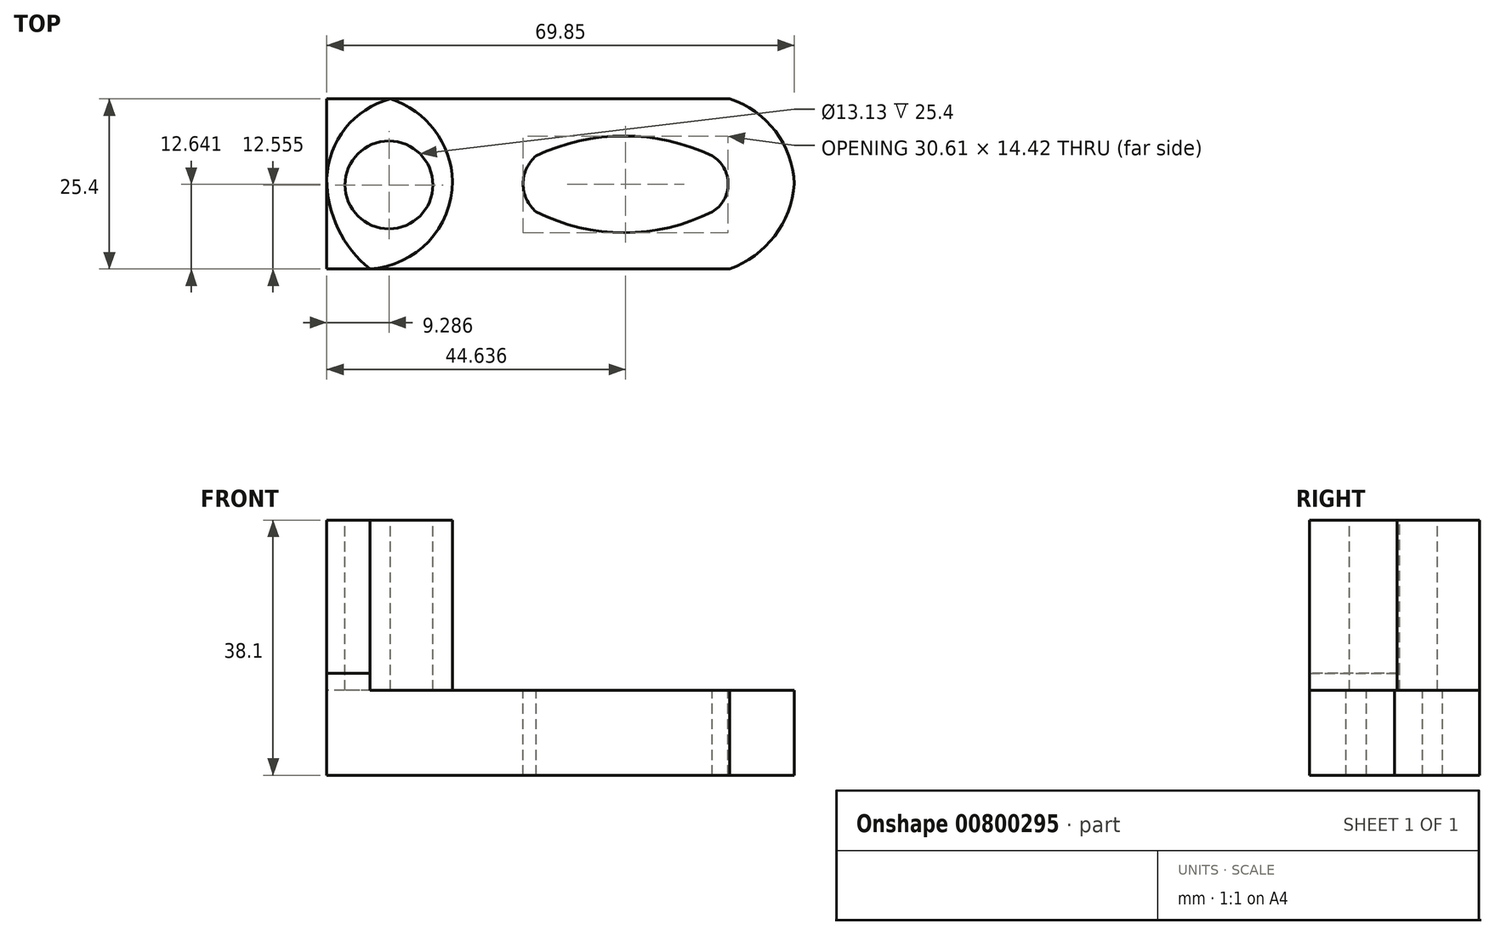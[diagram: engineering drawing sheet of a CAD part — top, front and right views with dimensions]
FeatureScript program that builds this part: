
annotation { "Feature Type Name" : "Feature", "Feature Type Description" : "" }
export const myFeature = defineFeature(function(context is Context, id is Id, definition is map)
    precondition{}
    {
        {
            var Q0;
            Q0=qCreatedBy(makeId("Front.planeOp"),FACE);
            var sketch = newSketch(context, id + "F0", { "sketchPlane" : qUnion([Q0])});
            skLineSegment(sketch, "E0", {"start": v(0, 0) * mm, "end": v(69.85, 0) * mm});
            skLineSegment(sketch, "E1", {"start": v(69.85, 0) * mm, "end": v(69.85, 12.7) * mm});
            skLineSegment(sketch, "E2", {"start": v(69.85, 12.7) * mm, "end": v(19.05, 12.7) * mm});
            skLineSegment(sketch, "E3", {"start": v(19.05, 12.7) * mm, "end": v(19.05, 38.1) * mm});
            skLineSegment(sketch, "E4", {"start": v(19.05, 38.1) * mm, "end": v(0, 38.1) * mm});
            skLineSegment(sketch, "E5", {"start": v(0, 38.1) * mm, "end": v(0, 0) * mm});
            skSolve(sketch);
        }
        {
            var Q0;
            Q0=makeQuery(id+"F0.imprint","IMPRINT",FACE,{"disambiguationData":[TD([[makeQuery(id+"F0.imprint","IMPRINT",EDGE,{"derivedFrom":sQuery(id+"F0.wireOp",EDGE,"E0")}),1.0]])]});
            extrude(context, id + "F1", {"entities" : qUnion([Q0]), "depth" : 25.4 * mm});
        }
        {
            var Q0;
            Q0=makeQuery(id+"F1.opExtrude","SWEPT_FACE",FACE,{"disambiguationData":[OSD([sQuery(id+"F0.wireOp",EDGE,"E2")])]});
            var sketch = newSketch(context, id + "F2", { "sketchPlane" : qUnion([Q0])});
            skArc(sketch, "E6", {"start": v(60.19, -25.4) * mm, "mid": v(66.88, -20.47) * mm, "end": v(69.85, -12.7) * mm});
            skArc(sketch, "E7", {"start": v(69.85, -12.7) * mm, "mid": v(67.02, -4.83) * mm, "end": v(60.19, 0) * mm});
            skSolve(sketch);
        }
        {
            var Q0;
            Q0=qSketchRegion(id+"F2",true);
            var Q1;
            {var subQ0=sQuery(id+"F2.wireOp",EDGE,"E7");Q1=makeQuery(id+"F2.imprint","IMPRINT",FACE,{"disambiguationData":[TD([[makeQuery(id+"F2.imprint","IMPRINT",EDGE,{"derivedFrom":subQ0}),-1.0]])]});}
            var Q2;
            {var subQ0=sQuery(id+"F2.wireOp",EDGE,"E6");Q2=makeQuery(id+"F2.imprint","IMPRINT",FACE,{"disambiguationData":[TD([[makeQuery(id+"F2.imprint","IMPRINT",EDGE,{"derivedFrom":subQ0}),-1.0]])]});}
            extrude(context, id + "F3", {"entities" : qUnion([Q0, Q1, Q2]), "operationType" : NewBodyOperationType.REMOVE, "oppositeDirection" : true, "depth" : 25.4 * mm});
        }
        {
            var Q0;
            Q0=makeQuery(id+"F1.opExtrude","SWEPT_FACE",FACE,{"disambiguationData":[OSD([sQuery(id+"F0.wireOp",EDGE,"E2")])]});
            var sketch = newSketch(context, id + "F4", { "sketchPlane" : qUnion([Q0])});
            skArc(sketch, "E8", {"start": v(31.26, -8.51) * mm, "mid": v(29.33, -12.7) * mm, "end": v(31.26, -16.87) * mm});
            skArc(sketch, "E9", {"start": v(57.57, -8.51) * mm, "mid": v(44.42, -5.55) * mm, "end": v(31.26, -8.51) * mm});
            skArc(sketch, "E10", {"start": v(57.57, -16.87) * mm, "mid": v(59.94, -12.7) * mm, "end": v(57.57, -8.51) * mm});
            skArc(sketch, "E11", {"start": v(31.26, -16.87) * mm, "mid": v(44.42, -19.97) * mm, "end": v(57.57, -16.87) * mm});
            skSolve(sketch);
        }
        {
            var Q0;
            Q0=makeQuery(id+"F4.imprint","IMPRINT",FACE,{"disambiguationData":[TD([[makeQuery(id+"F4.imprint","IMPRINT",EDGE,{"derivedFrom":sQuery(id+"F4.wireOp",EDGE,"E8")}),1.0]])]});
            extrude(context, id + "F5", {"entities" : qUnion([Q0]), "operationType" : NewBodyOperationType.REMOVE, "oppositeDirection" : true, "depth" : 25.4 * mm});
        }
        {
            var Q0;
            Q0=makeQuery(id+"F1.opExtrude","SWEPT_FACE",FACE,{"disambiguationData":[OSD([sQuery(id+"F0.wireOp",EDGE,"E4")])]});
            var sketch = newSketch(context, id + "F6", { "sketchPlane" : qUnion([Q0])});
            skCircle(sketch, "E12", {"center": v(9.29, -12.84) * mm, "radius": 6.57 * mm});
            skSolve(sketch);
        }
        {
            var Q0;
            Q0=makeQuery(id+"F6.imprint","IMPRINT",FACE,{"disambiguationData":[TD([[makeQuery(id+"F6.imprint","IMPRINT",EDGE,{"derivedFrom":sQuery(id+"F6.wireOp",EDGE,"E12")}),1.0]])]});
            extrude(context, id + "F7", {"entities" : qUnion([Q0]), "operationType" : NewBodyOperationType.REMOVE, "oppositeDirection" : true, "depth" : 25.4 * mm});
        }
        {
            var Q0;
            Q0=makeQuery(id+"F1.opExtrude","SWEPT_FACE",FACE,{"disambiguationData":[OSD([sQuery(id+"F0.wireOp",EDGE,"E4")])]});
            var sketch = newSketch(context, id + "F8", { "sketchPlane" : qUnion([Q0])});
            skArc(sketch, "E13", {"start": v(9.53, -25.4) * mm, "mid": v(18.79, -12.7) * mm, "end": v(9.53, 0) * mm});
            skSolve(sketch);
        }
        {
            var Q0;
            Q0=qSketchRegion(id+"F8",true);
            var Q1;
            {var subQ0=sQuery(id+"F8.wireOp",EDGE,"E13");Q1=makeQuery(id+"F8.imprint","IMPRINT",FACE,{"disambiguationData":[TD([[makeQuery(id+"F8.imprint","IMPRINT",EDGE,{"derivedFrom":subQ0}),-1.0]])]});}
            extrude(context, id + "F9", {"entities" : qUnion([Q0, Q1]), "operationType" : NewBodyOperationType.REMOVE, "oppositeDirection" : true, "depth" : 25.4 * mm});
        }
        {
            var Q0;
            Q0=makeQuery(id+"F1.opExtrude","SWEPT_FACE",FACE,{"disambiguationData":[OSD([sQuery(id+"F0.wireOp",EDGE,"E4")])]});
            var sketch = newSketch(context, id + "F10", { "sketchPlane" : qUnion([Q0])});
            skArc(sketch, "E14", {"start": v(9.53, 0) * mm, "mid": v(2.54, -4.68) * mm, "end": v(0, -12.7) * mm});
            skArc(sketch, "E15", {"start": v(4.76, -25.4) * mm, "mid": v(14.6, -21.88) * mm, "end": v(18.78, -12.32) * mm});
            skSolve(sketch);
        }
        {
            var Q0;
            Q0=qSketchRegion(id+"F10",true);
            var Q1;
            {var subQ1=sQuery(id+"F0.wireOp",EDGE,"E4");var subQ2=makeQuery(id+"F1.opExtrude","CAP_EDGE",EDGE,{"disambiguationData":[OSD([subQ1])],"isStart":true});Q1=makeQuery(id+"F10.imprint","IMPRINT",FACE,{"disambiguationData":[TD([[makeQuery(id+"F10.imprint","IMPRINT",EDGE,{"derivedFrom":subQ2}),1.0]])]});}
            var Q2;
            {var subQ0=sQuery(id+"F10.wireOp",EDGE,"E15");var subQ1=makeQuery(id+"F9.boolean.opBoolean","COPY",EDGE,{"derivedFrom":makeQuery(id+"F9.opExtrude","CAP_EDGE",EDGE,{"disambiguationData":[OSD([sQuery(id+"F8.wireOp",EDGE,"E13")])],"isStart":true})});var subQ2=makeQuery(id+"F10.imprint","INTERSECT",VERTEX,{"derivedFrom":[subQ1,subQ0]});Q2=makeQuery(id+"F10.imprint","IMPRINT",FACE,{"disambiguationData":[TD([[makeQuery(id+"F10.imprint","IMPRINT",EDGE,{"disambiguationData":[TD([[subQ2,1.0]])],"derivedFrom":subQ0}),-1.0]])]});}
            extrude(context, id + "F11", {"entities" : qUnion([Q0, Q1, Q2]), "operationType" : NewBodyOperationType.REMOVE, "oppositeDirection" : true, "depth" : 25.4 * mm});
        }
        {
            var Q0;
            Q0=makeQuery(id+"F1.opExtrude","SWEPT_FACE",FACE,{"disambiguationData":[OSD([sQuery(id+"F0.wireOp",EDGE,"E4")])]});
            var sketch = newSketch(context, id + "F12", { "sketchPlane" : qUnion([Q0])});
            skArc(sketch, "E16", {"start": v(0, -11.94) * mm, "mid": v(1.7, -19.4) * mm, "end": v(6.43, -25.4) * mm});
            skSolve(sketch);
        }
        {
            var Q0;
            Q0=makeQuery(id+"F12.imprint","IMPRINT",FACE,{"disambiguationData":[TD([[makeQuery(id+"F12.imprint","IMPRINT",EDGE,{"derivedFrom":sQuery(id+"F12.wireOp",EDGE,"E16")}),-1.0]])]});
            extrude(context, id + "F13", {"entities" : qUnion([Q0]), "operationType" : NewBodyOperationType.REMOVE, "oppositeDirection" : true, "depth" : 22.86 * mm});
        }
    });
